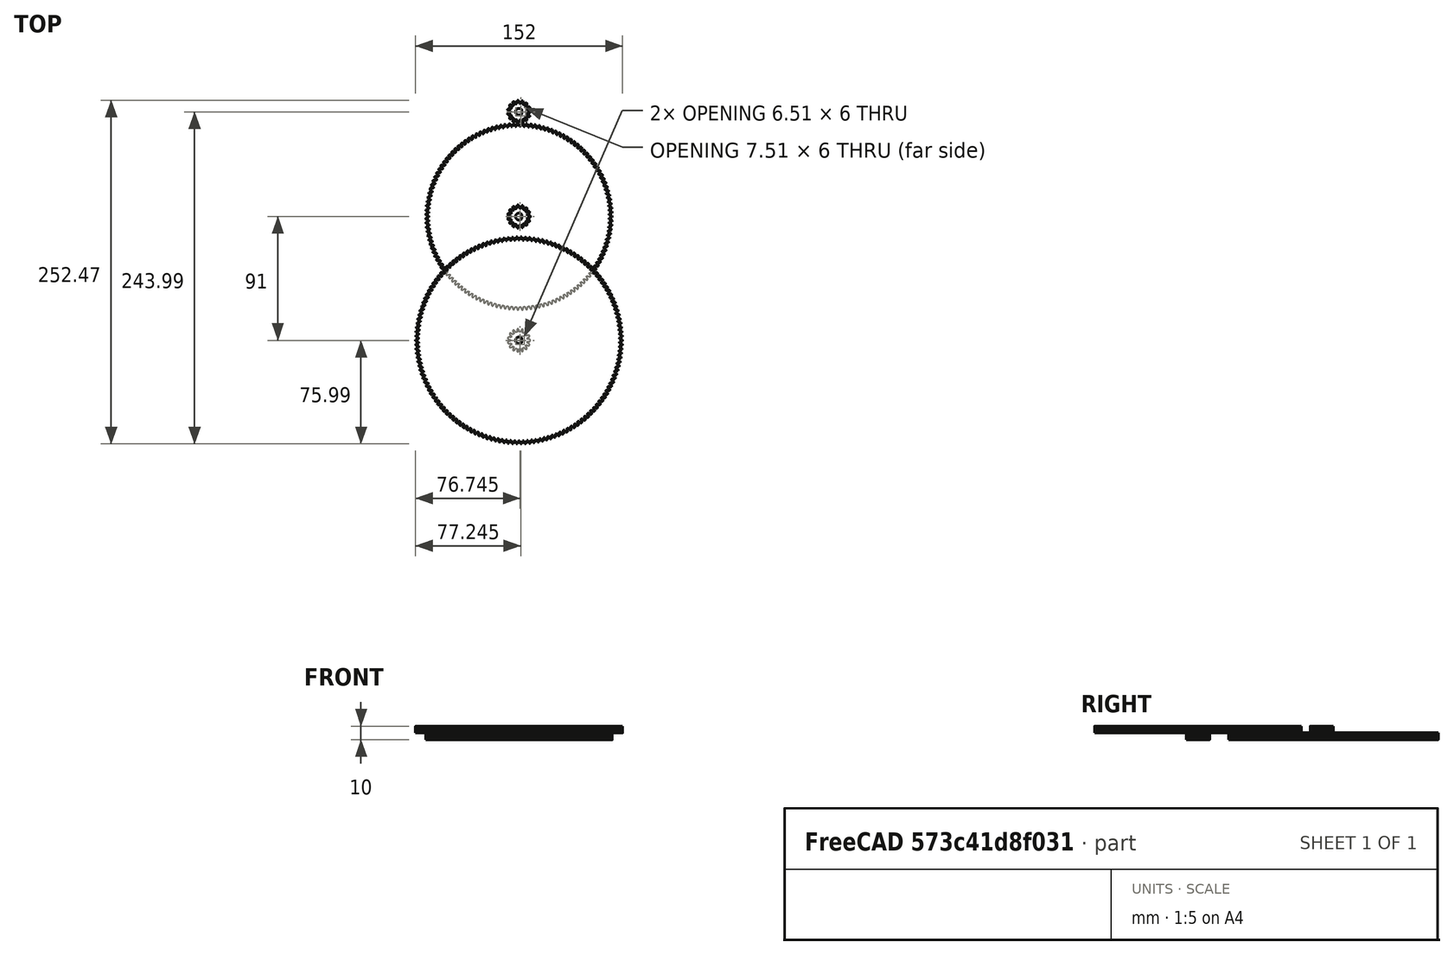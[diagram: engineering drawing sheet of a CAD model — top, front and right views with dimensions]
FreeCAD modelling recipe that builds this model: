
FCSTD DOCUMENT  (FreeCAD 0.20R29603 (Git))
Label: little-scout
License: All rights reserved
LicenseURL: http://en.wikipedia.org/wiki/All_rights_reserved
objects: Part::FeaturePython×13, Part::Cylinder×3, Part::Box×3
note: 19 computed .brp shape members not serialized (recipe doc carries the construction recipe); baked Part::Feature solids carry a one-line shape summary decoded from their .brp

FEATURE [Part::FeaturePython] InvoluteGear  # WARN: FeaturePython — macro-defined, semantics opaque (R4)
  AttacherType = Attacher::AttachEngine3D
  Placement = pos=(-200,50,0) rot=(0,0,1;0rad)
  angular_backlash = 0
  backlash = 0
  beta = 0
  clearance = 0.25
  da = 17
  df = 12.5
  double_helix = false
  dw = 15
  head = 0
  head_fillet = 0
  height = 5
  module = 1
  numpoints = 6
  pressure_angle = 20
  properties_from_tool = false
  reversed_backlash = false
  root_fillet = 0
  shift = 0
  simple = false
  teeth = 15
  transverse_pitch = 3.14159
  traverse_module = 1
  undercut = false
  version = 0.0.4
  expr: angular_backlash = backlash / dw * 360° / pi
FEATURE [Part::Cylinder] Cylinder
  Angle = 360
  AttacherType = Attacher::AttachEngine3D
  FirstAngle = 0
  Height = 5
  Placement = pos=(-200,50,0) rot=(0,0,1;0rad)
  Radius = 2.51
  SecondAngle = 0
FEATURE [Part::FeaturePython] InvoluteGear001  # WARN: FeaturePython — macro-defined, semantics opaque (R4)
  AttacherType = Attacher::AttachEngine3D
  angular_backlash = 0
  backlash = 0
  beta = 0
  clearance = 0.25
  da = 137
  df = 132.5
  double_helix = false
  dw = 135
  head = 0
  head_fillet = 0
  height = 5
  module = 1
  numpoints = 6
  pressure_angle = 20
  properties_from_tool = false
  reversed_backlash = false
  root_fillet = 0
  shift = 0
  simple = false
  teeth = 135
  transverse_pitch = 3.14159
  traverse_module = 1
  undercut = false
  version = 0.0.4
  expr: angular_backlash = backlash / dw * 360° / pi
FEATURE [Part::Cylinder] Cylinder001
  Angle = 360
  AttacherType = Attacher::AttachEngine3D
  FirstAngle = 0
  Height = 10
  Radius = 2.51
  SecondAngle = 0
FEATURE [Part::FeaturePython] InvoluteGear002  # WARN: FeaturePython — macro-defined, semantics opaque (R4)
  AttacherType = Attacher::AttachEngine3D
  Placement = pos=(0,0,5) rot=(0,0,1;0rad)
  angular_backlash = 0
  backlash = 0
  beta = 0
  clearance = 0.25
  da = 17
  df = 12.5
  double_helix = false
  dw = 15
  head = 0
  head_fillet = 0
  height = 5
  module = 1
  numpoints = 6
  pressure_angle = 20
  properties_from_tool = false
  reversed_backlash = false
  root_fillet = 0
  shift = 0
  simple = false
  teeth = 15
  transverse_pitch = 3.14159
  traverse_module = 1
  undercut = false
  version = 0.0.4
  expr: angular_backlash = backlash / dw * 360° / pi
FEATURE [Part::FeaturePython] Connect  # WARN: FeaturePython — macro-defined, semantics opaque (R4)
  Objects = -> [InvoluteGear001,InvoluteGear002]
  Tolerance = 0
FEATURE [Part::FeaturePython] Cutout001  label="Cutout"  # WARN: FeaturePython — macro-defined, semantics opaque (R4)
  Base = -> Connect
  Placement = pos=(-200,-40,0) rot=(0,0,1;0rad)
  Tolerance = 0
  Tool = -> Cylinder001
FEATURE [Part::Box] Box  label="Cube"
  AttacherType = Attacher::AttachEngine3D
  Height = 5
  Length = 3
  Placement = pos=(-198,47,0) rot=(0,0,1;0rad)
  Width = 6
FEATURE [Part::Box] Box001  label="Cube001"
  AttacherType = Attacher::AttachEngine3D
  Height = 10
  Length = 2
  Placement = pos=(-198,-43,0) rot=(0,0,1;0rad)
  Width = 6
FEATURE [Part::FeaturePython] Connect002  label="RaGear1"  # WARN: FeaturePython — macro-defined, semantics opaque (R4)
  Objects = -> [Cutout001,Box001]
  Tolerance = 0
FEATURE [Part::FeaturePython] Cutout  label="Cutout001"  # WARN: FeaturePython — macro-defined, semantics opaque (R4)
  Base = -> InvoluteGear
  Tolerance = 0
  Tool = -> Cylinder
FEATURE [Part::FeaturePython] Connect003  label="RaGear0"  # WARN: FeaturePython — macro-defined, semantics opaque (R4)
  Objects = -> [Cutout,Box]
  Placement = pos=(0,-13,0) rot=(0,0,1;0rad)
  Tolerance = 0
FEATURE [Part::FeaturePython] InvoluteGear003  # WARN: FeaturePython — macro-defined, semantics opaque (R4)
  AttacherType = Attacher::AttachEngine3D
  angular_backlash = 0
  backlash = 0
  beta = 0
  clearance = 0.25
  da = 152
  df = 147.5
  double_helix = false
  dw = 150
  head = 0
  head_fillet = 0
  height = 5
  module = 1
  numpoints = 6
  pressure_angle = 20
  properties_from_tool = false
  reversed_backlash = false
  root_fillet = 0
  shift = 0
  simple = false
  teeth = 150
  transverse_pitch = 3.14159
  traverse_module = 1
  undercut = false
  version = 0.0.4
  expr: angular_backlash = backlash / dw * 360° / pi
FEATURE [Part::FeaturePython] InvoluteGear004  # WARN: FeaturePython — macro-defined, semantics opaque (R4)
  AttacherType = Attacher::AttachEngine3D
  Placement = pos=(0,0,-5) rot=(0,0,1;0rad)
  angular_backlash = 0
  backlash = 0
  beta = 0
  clearance = 0.25
  da = 17
  df = 12.5
  double_helix = false
  dw = 15
  head = 0
  head_fillet = 0
  height = 5
  module = 1
  numpoints = 6
  pressure_angle = 20
  properties_from_tool = false
  reversed_backlash = false
  root_fillet = 0
  shift = 0
  simple = false
  teeth = 15
  transverse_pitch = 3.14159
  traverse_module = 1
  undercut = false
  version = 0.0.4
  expr: angular_backlash = backlash / dw * 360° / pi
FEATURE [Part::Cylinder] Cylinder002
  Angle = 360
  AttacherType = Attacher::AttachEngine3D
  FirstAngle = 0
  Height = 10
  Placement = pos=(0,0,-5) rot=(0,0,1;0rad)
  Radius = 2.51
  SecondAngle = 0
FEATURE [Part::Box] Box002  label="Cube002"
  AttacherType = Attacher::AttachEngine3D
  Height = 10
  Length = 2
  Placement = pos=(2,-3,-5) rot=(0,0,1;0rad)
  Width = 6
FEATURE [Part::FeaturePython] Connect004  # WARN: FeaturePython — macro-defined, semantics opaque (R4)
  Objects = -> [InvoluteGear004,InvoluteGear003]
  Tolerance = 0
FEATURE [Part::FeaturePython] Cutout002  # WARN: FeaturePython — macro-defined, semantics opaque (R4)
  Base = -> Connect004
  Tolerance = 0
  Tool = -> Cylinder002
FEATURE [Part::FeaturePython] Connect005  label="RaGear2"  # WARN: FeaturePython — macro-defined, semantics opaque (R4)
  Objects = -> [Cutout002,Box002]
  Placement = pos=(-200,-131,5) rot=(0,0,1;0rad)
  Tolerance = 0
